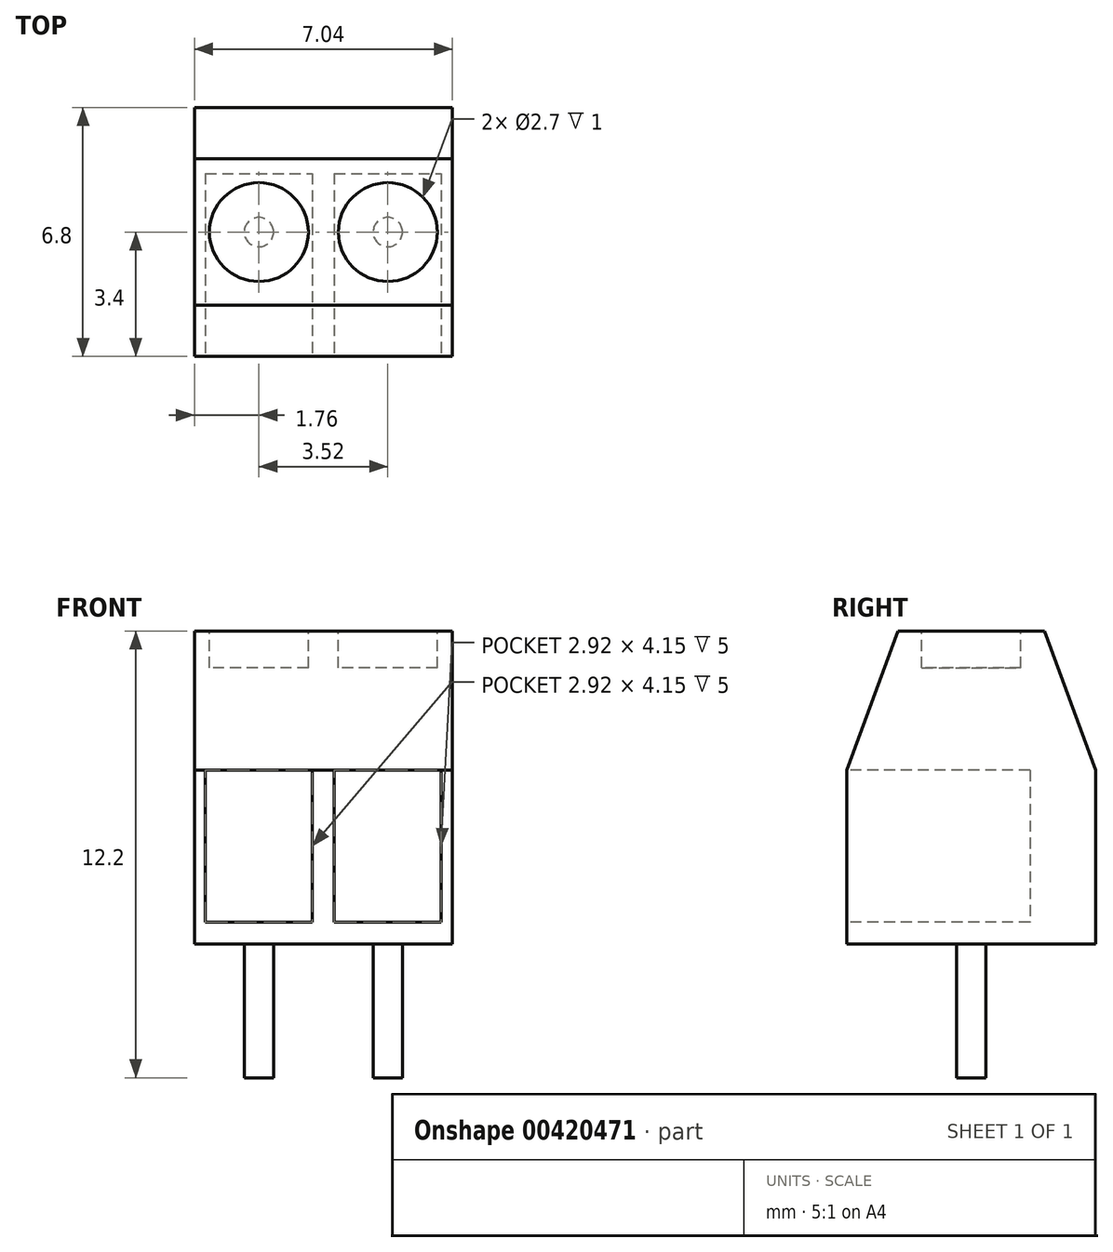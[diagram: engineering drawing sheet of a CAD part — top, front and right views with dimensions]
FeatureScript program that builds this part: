
annotation { "Feature Type Name" : "Feature", "Feature Type Description" : "" }
export const myFeature = defineFeature(function(context is Context, id is Id, definition is map)
    precondition{}
    {
        {
            var Q0;
            Q0=qCreatedBy(makeId("Front.planeOp"),FACE);
            var sketch = newSketch(context, id + "F0", { "sketchPlane" : qUnion([Q0])});
            skLineSegment(sketch, "E0.bottom", {"start": v(0, 0) * mm, "end": v(7.04, 0) * mm});
            skLineSegment(sketch, "E0.top", {"start": v(0, 8.55) * mm, "end": v(7.04, 8.55) * mm});
            skLineSegment(sketch, "E0.left", {"start": v(0, 0) * mm, "end": v(0, 8.55) * mm});
            skLineSegment(sketch, "E0.right", {"start": v(7.04, 0) * mm, "end": v(7.04, 8.55) * mm});
            skSolve(sketch);
        }
        {
            var Q0;
            Q0 = qSketchRegion(id + "F0", true);
            extrude(context, id + "F1", {"entities" : qUnion([Q0]), "depth" : 6.8 * mm});
        }
        {
            var Q0;
            Q0=makeQuery(id+"F1.opExtrude","SWEPT_FACE",FACE,{"disambiguationData":[OSD([sQuery(id+"F0.wireOp",EDGE,"E0.right")])]});
            var sketch = newSketch(context, id + "F2", { "sketchPlane" : qUnion([Q0])});
            skLineSegment(sketch, "E1", {"start": v(-3.4, 8.55) * mm, "end": v(-3.4, 0) * mm, "construction": true});
            skLineSegment(sketch, "E2", {"start": v(-6.8, 4.75) * mm, "end": v(-5.4, 8.55) * mm});
            skLineSegment(sketch, "E3", {"start": v(-5.4, 8.55) * mm, "end": v(-6.8, 8.55) * mm});
            skLineSegment(sketch, "E4", {"start": v(-6.8, 8.55) * mm, "end": v(-6.8, 4.75) * mm});
            skLineSegment(sketch, "E5.MirrorCS", {"start": v(0, 8.55) * mm, "end": v(0, 4.75) * mm});
            skLineSegment(sketch, "E6.MirrorCS", {"start": v(-1.4, 8.55) * mm, "end": v(0, 8.55) * mm});
            skLineSegment(sketch, "E7.MirrorCS", {"start": v(0, 4.75) * mm, "end": v(-1.4, 8.55) * mm});
            skSolve(sketch);
        }
        {
            var Q0;
            Q0 = qSketchRegion(id + "F2", true);
            extrude(context, id + "F3", {"entities" : qUnion([Q0]), "operationType" : NewBodyOperationType.REMOVE, "endBound" : BoundingType.UP_TO_NEXT, "oppositeDirection" : true, "depth" : 25 * mm});
        }
        {
            var Q0;
            Q0=makeQuery(id+"F1.opExtrude","CAP_FACE",FACE,{"disambiguationData":[OSD([sQuery(id+"F0.wireOp",EDGE,"E0.bottom"),sQuery(id+"F0.wireOp",EDGE,"E0.top"),sQuery(id+"F0.wireOp",EDGE,"E0.left"),sQuery(id+"F0.wireOp",EDGE,"E0.right")])],"isStart":false});
            var sketch = newSketch(context, id + "F4", { "sketchPlane" : qUnion([Q0])});
            skLineSegment(sketch, "E8", {"start": v(3.52, 4.75) * mm, "end": v(3.52, 0) * mm, "construction": true});
            skLineSegment(sketch, "E9.bottom", {"start": v(0.3, 4.75) * mm, "end": v(3.22, 4.75) * mm});
            skLineSegment(sketch, "E9.top", {"start": v(0.3, 0.6) * mm, "end": v(3.22, 0.6) * mm});
            skLineSegment(sketch, "E9.left", {"start": v(0.3, 4.75) * mm, "end": v(0.3, 0.6) * mm});
            skLineSegment(sketch, "E9.right", {"start": v(3.22, 4.75) * mm, "end": v(3.22, 0.6) * mm});
            skLineSegment(sketch, "E10.MirrorCS", {"start": v(3.82, 4.75) * mm, "end": v(3.82, 0.6) * mm});
            skLineSegment(sketch, "E11.MirrorCS", {"start": v(6.74, 4.75) * mm, "end": v(6.74, 0.6) * mm});
            skLineSegment(sketch, "E12.MirrorCS", {"start": v(6.74, 0.6) * mm, "end": v(3.82, 0.6) * mm});
            skLineSegment(sketch, "E13.MirrorCS", {"start": v(6.74, 4.75) * mm, "end": v(3.82, 4.75) * mm});
            skSolve(sketch);
        }
        {
            var Q0;
            Q0 = qSketchRegion(id + "F4", true);
            extrude(context, id + "F5", {"entities" : qUnion([Q0]), "operationType" : NewBodyOperationType.REMOVE, "oppositeDirection" : true, "depth" : 5 * mm});
        }
        {
            var Q0;
            Q0=makeQuery(id+"F1.opExtrude","SWEPT_FACE",FACE,{"disambiguationData":[OSD([sQuery(id+"F0.wireOp",EDGE,"E0.top")])]});
            var sketch = newSketch(context, id + "F6", { "sketchPlane" : qUnion([Q0])});
            skLineSegment(sketch, "E14", {"start": v(5.28, -1.4) * mm, "end": v(5.28, -5.4) * mm, "construction": true});
            skLineSegment(sketch, "E15", {"start": v(1.76, -1.4) * mm, "end": v(1.76, -5.4) * mm, "construction": true});
            skCircle(sketch, "E16", {"center": v(1.76, -3.4) * mm, "radius": 1.35 * mm});
            skCircle(sketch, "E17", {"center": v(5.28, -3.4) * mm, "radius": 1.35 * mm});
            skSolve(sketch);
        }
        {
            var Q0;
            Q0 = qSketchRegion(id + "F6", true);
            extrude(context, id + "F7", {"entities" : qUnion([Q0]), "operationType" : NewBodyOperationType.REMOVE, "oppositeDirection" : true, "depth" : 1 * mm});
        }
        {
            var Q0;
            Q0=makeQuery(id+"F1.opExtrude","SWEPT_FACE",FACE,{"disambiguationData":[OSD([sQuery(id+"F0.wireOp",EDGE,"E0.bottom")])]});
            var sketch = newSketch(context, id + "F8", { "sketchPlane" : qUnion([Q0])});
            skLineSegment(sketch, "E18", {"start": v(1.76, 6.8) * mm, "end": v(1.76, 0) * mm, "construction": true});
            skLineSegment(sketch, "E19", {"start": v(5.28, 6.8) * mm, "end": v(5.28, 0) * mm, "construction": true});
            skCircle(sketch, "E20", {"center": v(1.76, 3.4) * mm, "radius": 0.4 * mm});
            skCircle(sketch, "E21", {"center": v(5.28, 3.4) * mm, "radius": 0.4 * mm});
            skSolve(sketch);
        }
        {
            var Q0;
            Q0 = qSketchRegion(id + "F8", true);
            extrude(context, id + "F9", {"entities" : qUnion([Q0]), "operationType" : NewBodyOperationType.ADD, "depth" : 3.65 * mm});
        }
    });
